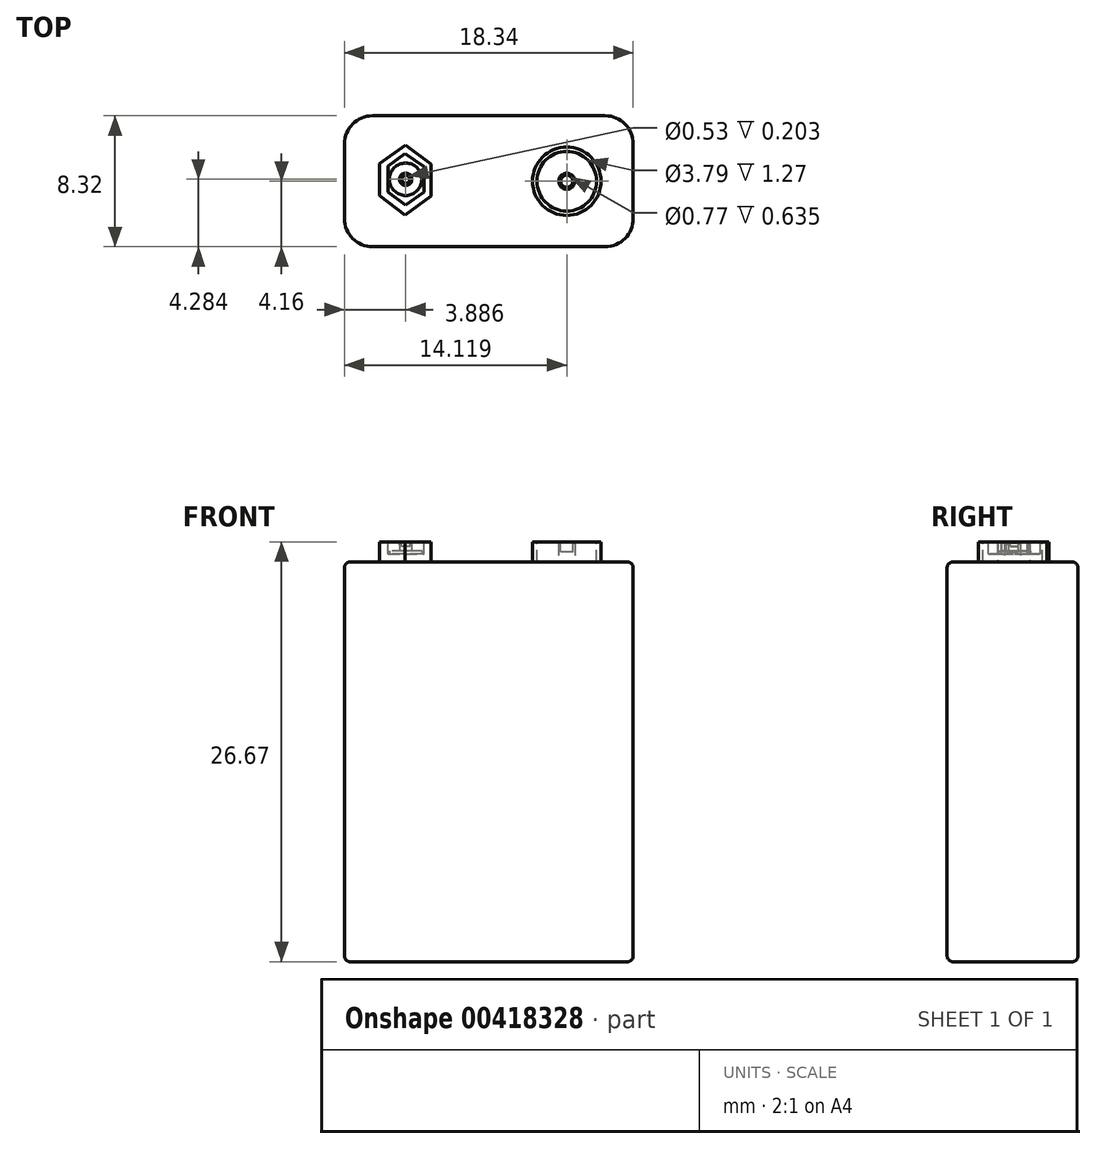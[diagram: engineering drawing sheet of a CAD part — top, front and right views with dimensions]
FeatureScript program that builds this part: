
annotation { "Feature Type Name" : "Feature", "Feature Type Description" : "" }
export const myFeature = defineFeature(function(context is Context, id is Id, definition is map)
    precondition{}
    {
        {
            var Q0;
            Q0=qCreatedBy(makeId("Top.planeOp"),FACE);
            var sketch = newSketch(context, id + "F0", { "sketchPlane" : qUnion([Q0])});
            skLineSegment(sketch, "E0.bottom", {"start": v(-7.4, -4.16) * mm, "end": v(7.4, -4.16) * mm});
            skLineSegment(sketch, "E0.top", {"start": v(-7.4, 4.16) * mm, "end": v(7.4, 4.16) * mm});
            skLineSegment(sketch, "E0.left", {"start": v(-9.17, -2.38) * mm, "end": v(-9.17, 2.38) * mm});
            skLineSegment(sketch, "E0.right", {"start": v(9.17, -2.38) * mm, "end": v(9.17, 2.38) * mm});
            skPoint(sketch, "E0.middle", {"position": v(0, 0) * mm});
            skPoint(sketch, "E1.visualSharp", {"position": v(9.17, 4.16) * mm});
            skArc(sketch, "E1.filletArc", {"start": v(9.17, 2.38) * mm, "mid": v(8.65, 3.63) * mm, "end": v(7.4, 4.16) * mm});
            skPoint(sketch, "E2.visualSharp", {"position": v(9.17, -4.16) * mm});
            skArc(sketch, "E2.filletArc", {"start": v(7.4, -4.16) * mm, "mid": v(8.65, -3.63) * mm, "end": v(9.17, -2.38) * mm});
            skPoint(sketch, "E3.visualSharp", {"position": v(-9.17, -4.16) * mm});
            skArc(sketch, "E3.filletArc", {"start": v(-9.17, -2.38) * mm, "mid": v(-8.65, -3.63) * mm, "end": v(-7.4, -4.16) * mm});
            skPoint(sketch, "E4.visualSharp", {"position": v(-9.17, 4.16) * mm});
            skArc(sketch, "E4.filletArc", {"start": v(-7.4, 4.16) * mm, "mid": v(-8.65, 3.63) * mm, "end": v(-9.17, 2.38) * mm});
            skSolve(sketch);
        }
        {
            var Q0;
            Q0 = qSketchRegion(id + "F0", true);
            extrude(context, id + "F1", {"entities" : qUnion([Q0]), "depth" : 25.4 * mm});
        }
        {
            var Q0;
            Q0=makeQuery(id+"F1.opExtrude","CAP_FACE",FACE,{"disambiguationData":[OSD([sQuery(id+"F0.wireOp",EDGE,"E0.bottom"),sQuery(id+"F0.wireOp",EDGE,"E0.top"),sQuery(id+"F0.wireOp",EDGE,"E0.left"),sQuery(id+"F0.wireOp",EDGE,"E0.right"),sQuery(id+"F0.wireOp",EDGE,"E1.filletArc"),sQuery(id+"F0.wireOp",EDGE,"E2.filletArc"),sQuery(id+"F0.wireOp",EDGE,"E3.filletArc"),sQuery(id+"F0.wireOp",EDGE,"E4.filletArc")])],"isStart":false});
            var sketch = newSketch(context, id + "F2", { "sketchPlane" : qUnion([Q0])});
            skLineSegment(sketch, "E5", {"start": v(-6.93, 1.11) * mm, "end": v(-5.29, 2.31) * mm});
            skLineSegment(sketch, "E6", {"start": v(-5.29, 2.31) * mm, "end": v(-3.67, 1.08) * mm});
            skLineSegment(sketch, "E7", {"start": v(-6.93, 1.11) * mm, "end": v(-6.93, -0.92) * mm});
            skLineSegment(sketch, "E8", {"start": v(-6.93, -0.92) * mm, "end": v(-5.31, -2.15) * mm});
            skLineSegment(sketch, "E9", {"start": v(-5.31, -2.15) * mm, "end": v(-3.67, -0.95) * mm});
            skLineSegment(sketch, "E10", {"start": v(-3.67, -0.95) * mm, "end": v(-3.67, 1.08) * mm});
            skSolve(sketch);
        }
        {
            var Q0;
            Q0=makeQuery(id+"F2.imprint","IMPRINT",FACE,{"disambiguationData":[TD([[makeQuery(id+"F2.imprint","IMPRINT",EDGE,{"derivedFrom":sQuery(id+"F2.wireOp",EDGE,"E5")}),-1.0]])]});
            extrude(context, id + "F3", {"entities" : qUnion([Q0]), "operationType" : NewBodyOperationType.ADD, "depth" : 1.27 * mm});
        }
        {
            var Q0;
            Q0=makeQuery(id+"F3.opExtrude","CAP_FACE",FACE,{"disambiguationData":[OSD([sQuery(id+"F2.wireOp",EDGE,"E5"),sQuery(id+"F2.wireOp",EDGE,"E6"),sQuery(id+"F2.wireOp",EDGE,"E7"),sQuery(id+"F2.wireOp",EDGE,"E8"),sQuery(id+"F2.wireOp",EDGE,"E9"),sQuery(id+"F2.wireOp",EDGE,"E10")])],"isStart":false});
            var sketch = newSketch(context, id + "F4", { "sketchPlane" : qUnion([Q0])});
            skLineSegment(sketch, "E11", {"start": v(-6.41, 0.97) * mm, "end": v(-5.32, 1.77) * mm});
            skLineSegment(sketch, "E12", {"start": v(-5.32, 1.77) * mm, "end": v(-4.12, 0.94) * mm});
            skLineSegment(sketch, "E13", {"start": v(-4.12, 0.94) * mm, "end": v(-4.12, -0.69) * mm});
            skLineSegment(sketch, "E14", {"start": v(-4.12, -0.69) * mm, "end": v(-5.29, -1.53) * mm});
            skLineSegment(sketch, "E15", {"start": v(-5.29, -1.53) * mm, "end": v(-6.41, -0.7) * mm});
            skLineSegment(sketch, "E16", {"start": v(-6.41, -0.7) * mm, "end": v(-6.41, 0.97) * mm});
            skSolve(sketch);
        }
        {
            var Q0;
            Q0=makeQuery(id+"F4.imprint","IMPRINT",FACE,{"disambiguationData":[TD([[makeQuery(id+"F4.imprint","IMPRINT",EDGE,{"derivedFrom":sQuery(id+"F4.wireOp",EDGE,"E11")}),-1.0]])]});
            extrude(context, id + "F5", {"entities" : qUnion([Q0]), "operationType" : NewBodyOperationType.REMOVE, "oppositeDirection" : true, "depth" : 0.76 * mm});
        }
        {
            var Q0;
            Q0=makeQuery(id+"F5.boolean.opBoolean","COPY",FACE,{"derivedFrom":makeQuery(id+"F5.opExtrude","CAP_FACE",FACE,{"disambiguationData":[OSD([sQuery(id+"F4.wireOp",EDGE,"E11"),sQuery(id+"F4.wireOp",EDGE,"E12"),sQuery(id+"F4.wireOp",EDGE,"E13"),sQuery(id+"F4.wireOp",EDGE,"E14"),sQuery(id+"F4.wireOp",EDGE,"E15"),sQuery(id+"F4.wireOp",EDGE,"E16")])],"isStart":false})});
            var sketch = newSketch(context, id + "F6", { "sketchPlane" : qUnion([Q0])});
            skCircle(sketch, "E17", {"center": v(-5.28, 0.12) * mm, "radius": 1.03 * mm});
            skPoint(sketch, "E17.centerSnap0", {"position": v(-4.12, 0.12) * mm});
            skSolve(sketch);
        }
        {
            var Q0;
            Q0=makeQuery(id+"F6.imprint","IMPRINT",FACE,{"disambiguationData":[TD([[makeQuery(id+"F6.imprint","IMPRINT",EDGE,{"derivedFrom":sQuery(id+"F6.wireOp",EDGE,"E17")}),1.0]])]});
            extrude(context, id + "F7", {"entities" : qUnion([Q0]), "operationType" : NewBodyOperationType.ADD, "depth" : 0.18 * mm});
        }
        {
            var Q0;
            Q0=makeQuery(id+"F7.opExtrude","CAP_FACE",FACE,{"disambiguationData":[OSD([sQuery(id+"F6.wireOp",EDGE,"E17")])],"isStart":false});
            var sketch = newSketch(context, id + "F8", { "sketchPlane" : qUnion([Q0])});
            skCircle(sketch, "E18", {"center": v(-5.28, 0.12) * mm, "radius": 0.39 * mm});
            skSolve(sketch);
        }
        {
            var Q0;
            Q0=makeQuery(id+"F8.imprint","IMPRINT",FACE,{"disambiguationData":[TD([[makeQuery(id+"F8.imprint","IMPRINT",EDGE,{"derivedFrom":sQuery(id+"F8.wireOp",EDGE,"E18")}),1.0]])]});
            extrude(context, id + "F9", {"entities" : qUnion([Q0]), "operationType" : NewBodyOperationType.ADD, "depth" : 0.5 * mm});
        }
        {
            var Q0;
            Q0=makeQuery(id+"F9.opExtrude","CAP_EDGE",EDGE,{"disambiguationData":[OSD([sQuery(id+"F8.wireOp",EDGE,"E18")])],"isStart":false});
            fillet(context, id + "F10", {"entities" : qUnion([Q0]), "radius" : 0.12 * mm, "tangentPropagation" : true, "rho" : 0.5, "crossSection" : FilletCrossSection.CONIC, "allowEdgeOverflow" : false});
        }
        {
            var Q0;
            Q0=makeQuery(id+"F9.opExtrude","CAP_FACE",FACE,{"disambiguationData":[OSD([sQuery(id+"F8.wireOp",EDGE,"E18")])],"isStart":false});
            extrude(context, id + "F11", {"entities" : qUnion([Q0]), "operationType" : NewBodyOperationType.REMOVE, "oppositeDirection" : true, "depth" : 0.2 * mm});
        }
        {
            var Q0;
            Q0=makeQuery(id+"F1.opExtrude","CAP_FACE",FACE,{"disambiguationData":[OSD([sQuery(id+"F0.wireOp",EDGE,"E0.bottom"),sQuery(id+"F0.wireOp",EDGE,"E0.top"),sQuery(id+"F0.wireOp",EDGE,"E0.left"),sQuery(id+"F0.wireOp",EDGE,"E0.right"),sQuery(id+"F0.wireOp",EDGE,"E1.filletArc"),sQuery(id+"F0.wireOp",EDGE,"E2.filletArc"),sQuery(id+"F0.wireOp",EDGE,"E3.filletArc"),sQuery(id+"F0.wireOp",EDGE,"E4.filletArc")])],"isStart":false});
            var sketch = newSketch(context, id + "F12", { "sketchPlane" : qUnion([Q0])});
            skCircle(sketch, "E19", {"center": v(4.95, 0) * mm, "radius": 2.17 * mm});
            skSolve(sketch);
        }
        {
            var Q0;
            Q0 = qSketchRegion(id + "F12", true);
            extrude(context, id + "F13", {"entities" : qUnion([Q0]), "operationType" : NewBodyOperationType.ADD, "depth" : 1.27 * mm});
        }
        {
            var Q0;
            Q0=makeQuery(id+"F13.opExtrude","CAP_FACE",FACE,{"disambiguationData":[OSD([sQuery(id+"F12.wireOp",EDGE,"E19")])],"isStart":false});
            var sketch = newSketch(context, id + "F14", { "sketchPlane" : qUnion([Q0])});
            skCircle(sketch, "E20", {"center": v(4.95, 0) * mm, "radius": 1.9 * mm});
            skSolve(sketch);
        }
        {
            var Q0;
            Q0=makeQuery(id+"F14.imprint","IMPRINT",FACE,{"disambiguationData":[TD([[makeQuery(id+"F14.imprint","IMPRINT",EDGE,{"derivedFrom":sQuery(id+"F14.wireOp",EDGE,"E20")}),1.0]])]});
            extrude(context, id + "F15", {"entities" : qUnion([Q0]), "operationType" : NewBodyOperationType.REMOVE, "oppositeDirection" : true, "depth" : 1.27 * mm});
        }
        {
            var Q0;
            Q0=makeQuery(id+"F15.boolean.opBoolean","COPY",FACE,{"derivedFrom":makeQuery(id+"F15.opExtrude","CAP_FACE",FACE,{"disambiguationData":[OSD([sQuery(id+"F14.wireOp",EDGE,"E20")])],"isStart":false})});
            var sketch = newSketch(context, id + "F16", { "sketchPlane" : qUnion([Q0])});
            skCircle(sketch, "E21", {"center": v(4.95, 0) * mm, "radius": 0.5 * mm});
            skSolve(sketch);
        }
        {
            var Q0;
            Q0=makeQuery(id+"F16.imprint","IMPRINT",FACE,{"disambiguationData":[TD([[makeQuery(id+"F16.imprint","IMPRINT",EDGE,{"derivedFrom":sQuery(id+"F16.wireOp",EDGE,"E21")}),1.0]])]});
            extrude(context, id + "F17", {"entities" : qUnion([Q0]), "operationType" : NewBodyOperationType.ADD, "depth" : 1.27 * mm});
        }
        {
            var Q0;
            Q0=makeQuery(id+"F17.opExtrude","CAP_EDGE",EDGE,{"disambiguationData":[OSD([sQuery(id+"F16.wireOp",EDGE,"E21")])],"isStart":false});
            fillet(context, id + "F18", {"entities" : qUnion([Q0]), "radius" : 0.12 * mm, "tangentPropagation" : true, "allowEdgeOverflow" : false});
        }
        {
            var Q0;
            Q0=makeQuery(id+"F17.opExtrude","CAP_FACE",FACE,{"disambiguationData":[OSD([sQuery(id+"F16.wireOp",EDGE,"E21")])],"isStart":false});
            extrude(context, id + "F19", {"entities" : qUnion([Q0]), "operationType" : NewBodyOperationType.REMOVE, "oppositeDirection" : true, "depth" : 0.64 * mm});
        }
        {
            var Q0;
            Q0=makeQuery(id+"F1.opExtrude","CAP_EDGE",EDGE,{"disambiguationData":[OSD([sQuery(id+"F0.wireOp",EDGE,"E0.bottom")])],"isStart":false});
            var Q1;
            Q1=makeQuery(id+"F1.opExtrude","CAP_EDGE",EDGE,{"disambiguationData":[OSD([sQuery(id+"F0.wireOp",EDGE,"E0.top")])],"isStart":false});
            fillet(context, id + "F20", {"entities" : qUnion([Q0, Q1]), "radius" : 0.38 * mm, "tangentPropagation" : true, "allowEdgeOverflow" : false});
        }
        {
            var Q0;
            Q0=makeQuery(id+"F1.opExtrude","CAP_EDGE",EDGE,{"disambiguationData":[OSD([sQuery(id+"F0.wireOp",EDGE,"E0.top")])],"isStart":true});
            fillet(context, id + "F21", {"entities" : qUnion([Q0]), "radius" : 0.38 * mm, "tangentPropagation" : true, "allowEdgeOverflow" : false});
        }
    });
